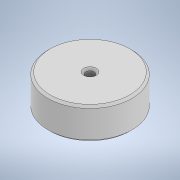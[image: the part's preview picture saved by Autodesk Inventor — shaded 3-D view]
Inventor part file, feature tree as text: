
AUTODESK INVENTOR PART (.ipt)
format: ipt  version: 2021 (Build 250183000, 183)  size: 113,152 bytes
history: native  units: mm
features: extrude x2, chamfer x2, sketch x2
ambient origin geometry x8: Origin, YZ Plane, XZ Plane, XY Plane, X Axis, Y Axis, Z Axis, Center Point
bodies: Solid1 (feature_tree)
feature tree (6):
  extrude  "Extrusion1"  Depth=75.0mm TaperAngle=0.0deg
  chamfer  "Chamfer1"  Distance=5.0mm Angle=45.0deg
  extrude  "Extrusion2"  Depth=75.0mm TaperAngle=0.0deg
  chamfer  "Chamfer2"  Distance=5.0mm Angle=45.0deg
  sketch  "Sketch1"  dims[d0=200.0mm d1=75.0mm d2=0.0mm d3=5.0mm d4=2.0mm d5=45.0deg]
  sketch  "Sketch2"  dims[d6=20.0mm d7=75.0mm d8=0.0mm d9=5.0mm d10=2.0mm d11=45.0deg]
